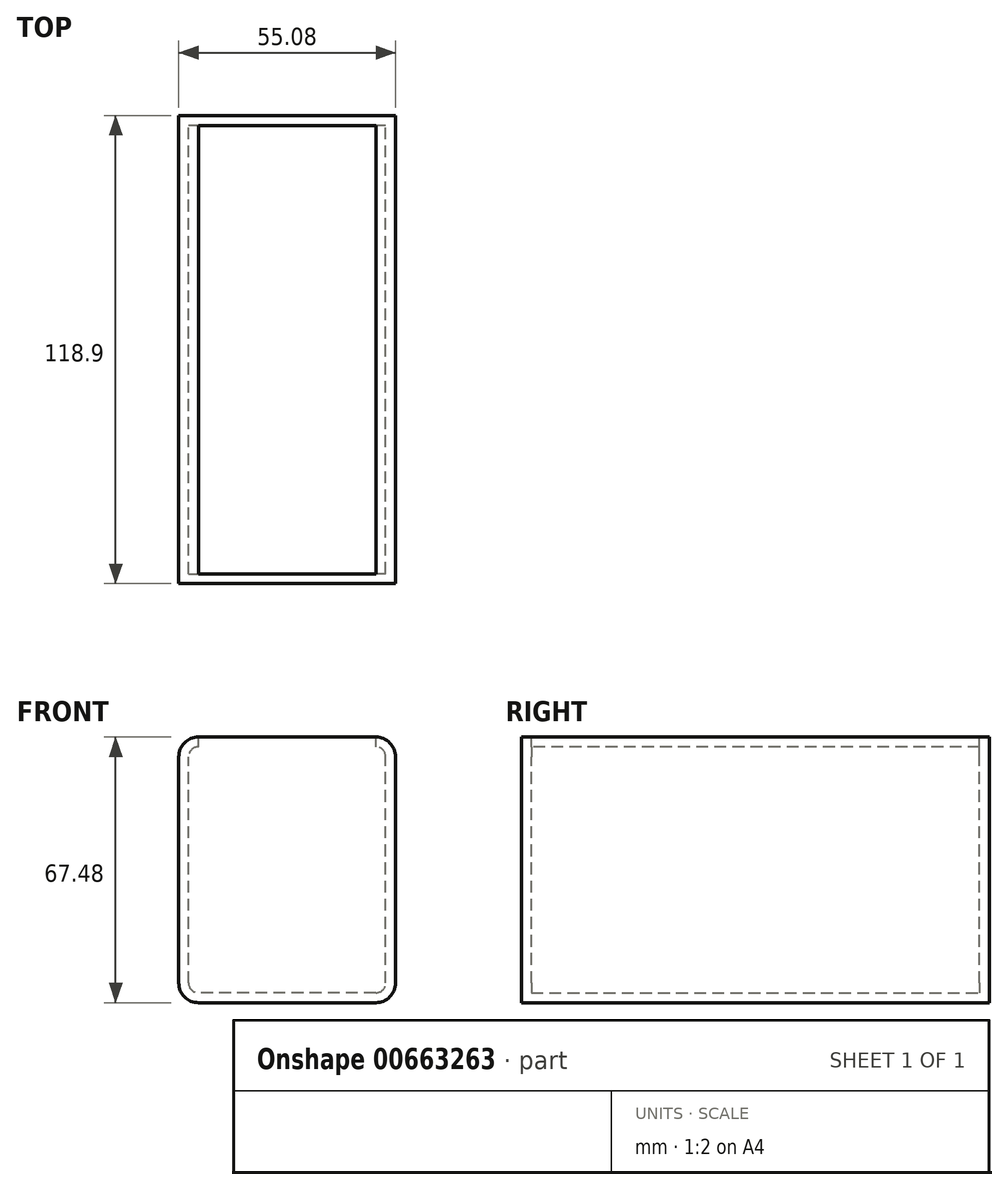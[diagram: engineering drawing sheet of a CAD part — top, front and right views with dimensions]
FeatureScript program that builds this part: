
annotation { "Feature Type Name" : "Feature", "Feature Type Description" : "" }
export const myFeature = defineFeature(function(context is Context, id is Id, definition is map)
    precondition{}
    {
        {
            var Q0;
            Q0=qCreatedBy(makeId("Front.planeOp"),FACE);
            var sketch = newSketch(context, id + "F0", { "sketchPlane" : qUnion([Q0])});
            skLineSegment(sketch, "E0.bottom", {"start": v(27.54, -33.74) * mm, "end": v(-27.54, -33.74) * mm});
            skLineSegment(sketch, "E0.top", {"start": v(27.54, 33.74) * mm, "end": v(-27.54, 33.74) * mm});
            skLineSegment(sketch, "E0.left", {"start": v(27.54, -33.74) * mm, "end": v(27.54, 33.74) * mm});
            skLineSegment(sketch, "E0.right", {"start": v(-27.54, -33.74) * mm, "end": v(-27.54, 33.74) * mm});
            skPoint(sketch, "E0.middle", {"position": v(0, 0) * mm});
            skSolve(sketch);
        }
        {
            var Q0;
            Q0=qSketchRegion(id+"F0",true);
            extrude(context, id + "F1", {"entities" : qUnion([Q0]), "depth" : 118.9 * mm, "offsetDistance" : 25 * mm});
        }
        {
            var Q0;
            Q0=makeQuery(id+"F1.opExtrude","SWEPT_EDGE",EDGE,{"disambiguationData":[OSD([sQuery(id+"F0.wireOp",EDGE,"E0.top"),sQuery(id+"F0.wireOp",EDGE,"E0.right")])]});
            var Q1;
            Q1=makeQuery(id+"F1.opExtrude","SWEPT_EDGE",EDGE,{"disambiguationData":[OSD([sQuery(id+"F0.wireOp",EDGE,"E0.top"),sQuery(id+"F0.wireOp",EDGE,"E0.left")])]});
            var Q2;
            Q2=makeQuery(id+"F1.opExtrude","SWEPT_EDGE",EDGE,{"disambiguationData":[OSD([sQuery(id+"F0.wireOp",EDGE,"E0.bottom"),sQuery(id+"F0.wireOp",EDGE,"E0.right")])]});
            var Q3;
            Q3=makeQuery(id+"F1.opExtrude","SWEPT_EDGE",EDGE,{"disambiguationData":[OSD([sQuery(id+"F0.wireOp",EDGE,"E0.bottom"),sQuery(id+"F0.wireOp",EDGE,"E0.left")])]});
            fillet(context, id + "F2", {"entities" : qUnion([Q0, Q1, Q2, Q3]), "radius" : 5 * mm, "tangentPropagation" : true, "allowEdgeOverflow" : false});
        }
        {
            var Q0;
            Q0=makeQuery(id+"F1.opExtrude","SWEPT_FACE",FACE,{"disambiguationData":[OSD([sQuery(id+"F0.wireOp",EDGE,"E0.top")])]});
            shell(context, id + "F3", {"entities" : qUnion([Q0]), "thickness" : 2.5 * mm});
        }
    });
